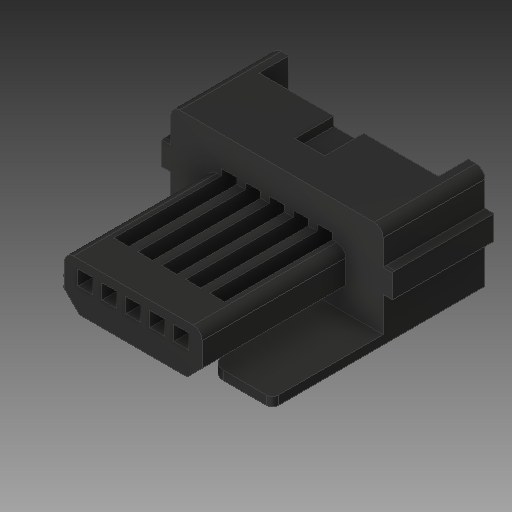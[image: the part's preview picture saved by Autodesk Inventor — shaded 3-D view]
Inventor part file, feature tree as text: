
AUTODESK INVENTOR PART (.ipt)
format: ipt  version: 2019 (Build 230136000, 136)  size: 201,728 bytes
history: native  units: in
note: dims shown in document units (in); Inventor stores cm internally (conversion verified against a paired STEP export)
features: fillet x1
ambient origin geometry x8: Origin, YZ Plane, XZ Plane, XY Plane, X Axis, Y Axis, Z Axis, Center Point
bodies: Solid1 (feature_tree)
feature tree (1):
  fillet  "Fillet3"  [1 undecoded]
note: 1 required parameter value undecoded (feature->parameter linkage not recoverable at this tier; creation-order binding heuristic only, values carry confidence <= 0.55)
